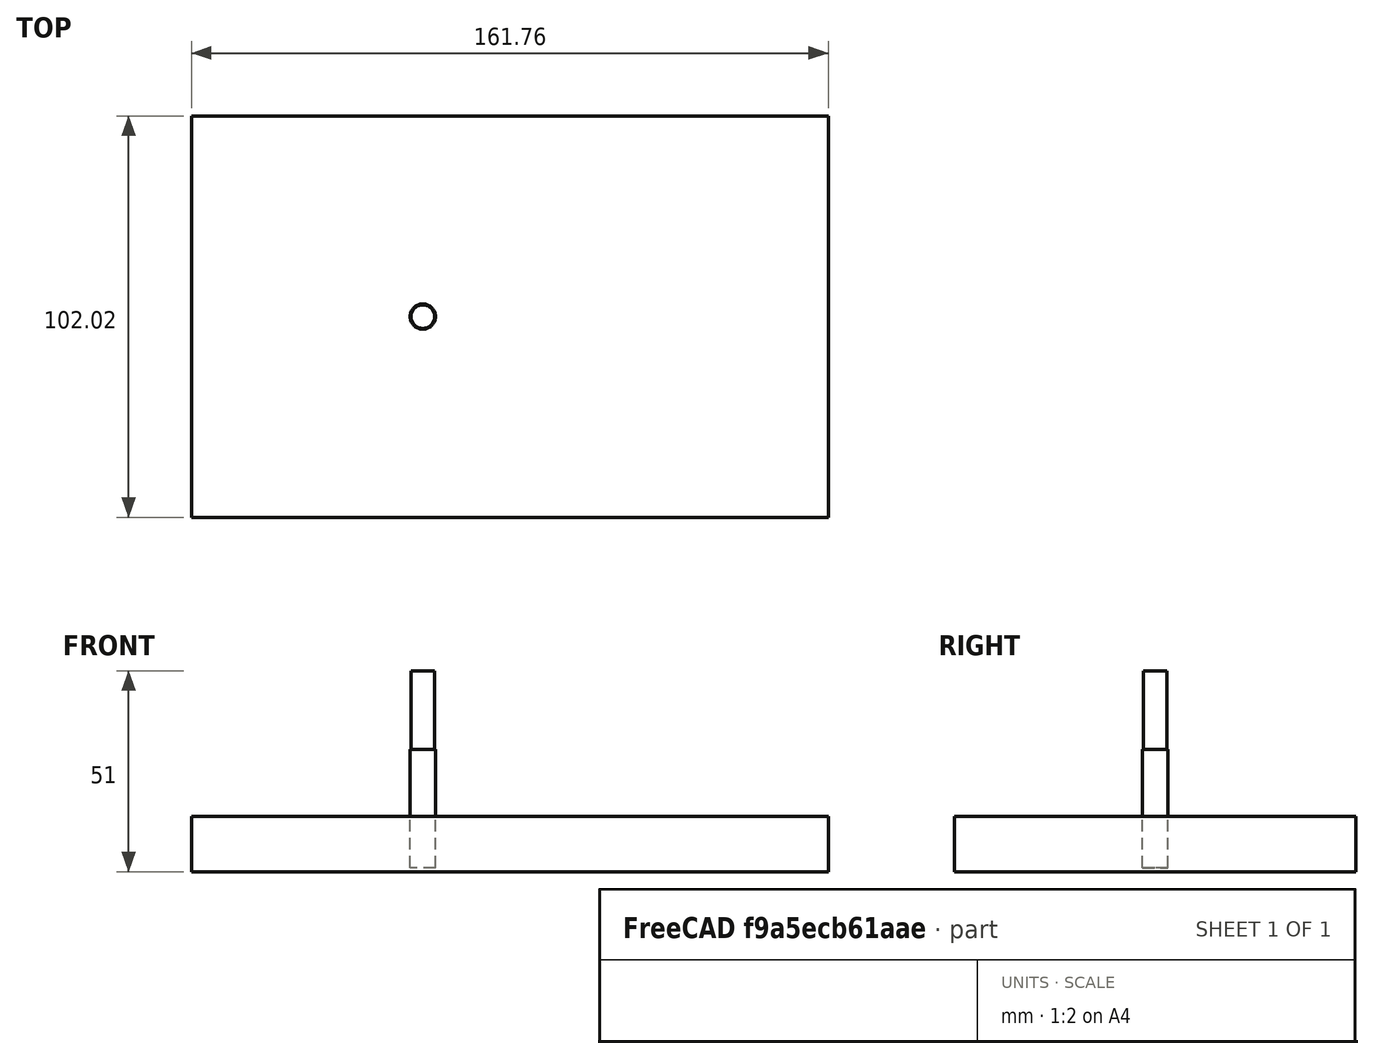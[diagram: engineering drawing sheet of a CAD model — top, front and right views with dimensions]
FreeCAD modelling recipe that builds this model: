
FCSTD DOCUMENT  (FreeCAD 0.20R27465 (Git))
Label: DemoFit
License: All rights reserved
LicenseURL: http://en.wikipedia.org/wiki/All_rights_reserved
objects: Part::FeaturePython×5, Path::FeaturePython×5, Sketcher::SketchObject×3, PartDesign::Pad×3, PartDesign::Fillet×3, PartDesign::Body×3, Mesh::FeaturePython×3, App::DocumentObjectGroup×2, App::FeaturePython×1, Path::FeatureCompoundPython×1
note: 26 computed .brp shape members not serialized (recipe doc carries the construction recipe); baked Part::Feature solids carry a one-line shape summary decoded from their .brp

FEATURE [Sketcher::SketchObject] Sketch
  FullyConstrained = true
  MapMode = 5
  Support = -> [XY_Plane]
  sketch-geometry (24):
    g0: LineSegment StartX=-57.735 StartY=0 StartZ=0 EndX=-28.8675 EndY=-50 EndZ=0
    g1: LineSegment StartX=-28.8675 StartY=-50 StartZ=0 EndX=28.8675 EndY=-50 EndZ=0
    g2: LineSegment StartX=28.8675 StartY=-50 StartZ=0 EndX=57.735 EndY=0 EndZ=0
    g3: LineSegment StartX=57.735 StartY=0 StartZ=0 EndX=28.8675 EndY=50 EndZ=0
    g4: LineSegment StartX=28.8675 StartY=50 StartZ=0 EndX=-28.8675 EndY=50 EndZ=0
    g5: LineSegment StartX=-28.8675 StartY=50 StartZ=0 EndX=-57.735 EndY=0 EndZ=0
    g6: Circle CenterX=0 CenterY=0 CenterZ=0 NormalX=0 NormalY=0 NormalZ=1 AngleXU=0 Radius=57.735
    g7: LineSegment StartX=-30.0067 StartY=21.9359 StartZ=0 EndX=-45.2718 EndY=9.76238 EndZ=0
    g8: LineSegment StartX=-45.2718 StartY=9.76238 StartZ=0 EndX=-45.2718 EndY=-9.76238 EndZ=0
    g9: LineSegment StartX=-45.2718 StartY=-9.76238 StartZ=0 EndX=-30.0067 EndY=-21.9359 EndZ=0
    g10: LineSegment StartX=-30.0067 StartY=-21.9359 StartZ=0 EndX=-10.9715 EndY=-17.5912 EndZ=0
    g11: LineSegment StartX=-10.9715 StartY=-17.5912 StartZ=0 EndX=-2.5 EndY=0 EndZ=0
    g12: LineSegment StartX=-2.5 StartY=0 StartZ=0 EndX=-10.9715 EndY=17.5912 EndZ=0
    g13: LineSegment StartX=-10.9715 StartY=17.5912 StartZ=0 EndX=-30.0067 EndY=21.9359 EndZ=0
    g14: Circle CenterX=-25 CenterY=0 CenterZ=0 NormalX=0 NormalY=0 NormalZ=1 AngleXU=0 Radius=22.5
    g15: LineSegment StartX=25 StartY=22.5 StartZ=0 EndX=9.0901 EndY=15.9099 EndZ=0
    g16: LineSegment StartX=9.0901 StartY=15.9099 StartZ=0 EndX=2.5 EndY=0 EndZ=0
    g17: LineSegment StartX=2.5 StartY=0 StartZ=0 EndX=9.0901 EndY=-15.9099 EndZ=0
    g18: LineSegment StartX=9.0901 StartY=-15.9099 StartZ=0 EndX=25 EndY=-22.5 EndZ=0
    g19: LineSegment StartX=25 StartY=-22.5 StartZ=0 EndX=40.9099 EndY=-15.9099 EndZ=0
    g20: LineSegment StartX=40.9099 StartY=-15.9099 StartZ=0 EndX=47.5 EndY=-3.6e-15 EndZ=0
    g21: LineSegment StartX=47.5 StartY=-3.6e-15 StartZ=0 EndX=40.9099 EndY=15.9099 EndZ=0
    g22: LineSegment StartX=40.9099 StartY=15.9099 StartZ=0 EndX=25 EndY=22.5 EndZ=0
    g23: Circle CenterX=25 CenterY=0 CenterZ=0 NormalX=0 NormalY=0 NormalZ=1 AngleXU=0 Radius=22.5
  constraints (56):
    c: Coincident(g0,g1)
    c: Coincident(g1,g2)
    c: Coincident(g2,g3)
    c: Coincident(g3,g4)
    c: Coincident(g4,g5)
    c: Coincident(g5,g0)
    c: Equal(g0, g1-g5) x5
    c: PointOnObject(g0,g6)
    c: PointOnObject(g1,g6)
    c: PointOnObject(g2,g6)
    c: PointOnObject(g3,g6)
    c: PointOnObject(g4,g6)
    c: PointOnObject(g5,g6)
    c: Coincident(g6,g-1)
    c: DistanceY(g-1,g2) = 0
    c: DistanceY(g-1,g4) = 50
    c: Coincident(g7,g8)
    c: Coincident(g8,g9)
    c: Coincident(g9,g10)
    c: Coincident(g10,g11)
    c: Coincident(g11,g12)
    c: Coincident(g12,g13)
    c: Coincident(g13,g7)
    c: Equal(g7, g8-g13) x6
    c: PointOnObject(g7,g14)
    c: PointOnObject(g8,g14)
    c: PointOnObject(g9,g14)
    c: PointOnObject(g10,g14)
    c: PointOnObject(g11,g14)
    c: PointOnObject(g12,g14)
    c: PointOnObject(g13,g14)
    c: DistanceY(g-1,g14) = 0
    c: DistanceX(g14,g-1) = 25
    c: Diameter(g14) = 45
    c: DistanceY(g-1,g11) = 0
    c: Coincident(g15,g16)
    c: Coincident(g16,g17)
    c: Coincident(g17,g18)
    c: Coincident(g18,g19)
    c: Coincident(g19,g20)
    c: Coincident(g20,g21)
    c: Coincident(g21,g22)
    c: Coincident(g22,g15)
    c: Equal(g15, g16-g22) x7
    c: PointOnObject(g15,g23)
    c: PointOnObject(g16,g23)
    c: PointOnObject(g17,g23)
    c: PointOnObject(g18,g23)
    c: PointOnObject(g19,g23)
    c: PointOnObject(g20,g23)
    c: PointOnObject(g21,g23)
    c: PointOnObject(g22,g23)
    c: DistanceX(g-1,g23) = 25
    c: DistanceY(g-1,g23) = 0
    c: Diameter(g23) = 45
    c: DistanceY(g-1,g16) = 0
FEATURE [PartDesign::Pad] Pad
  Direction = (1,1,1)
  Length = 12
  Length2 = 100
  Profile = -> Sketch
  Refine = true
  Type = 0
FEATURE [Sketcher::SketchObject] Sketch001
  FullyConstrained = true
  MapMode = 5
  Support = -> [XY_Plane001]
  sketch-geometry (8):
    g0: LineSegment StartX=100.227 StartY=15.2593 StartZ=0 EndX=100.227 EndY=34.7407 EndZ=0
    g1: LineSegment StartX=100.227 StartY=34.7407 StartZ=0 EndX=84.9956 EndY=46.8871 EndZ=0
    g2: LineSegment StartX=84.9956 StartY=46.8871 StartZ=0 EndX=66.0027 EndY=42.5521 EndZ=0
    g3: LineSegment StartX=66.0027 StartY=42.5521 StartZ=0 EndX=57.55 EndY=25 EndZ=0
    g4: LineSegment StartX=57.55 StartY=25 StartZ=0 EndX=66.0027 EndY=7.44788 EndZ=0
    g5: LineSegment StartX=66.0027 StartY=7.44788 StartZ=0 EndX=84.9956 EndY=3.11287 EndZ=0
    g6: LineSegment StartX=84.9956 StartY=3.11287 StartZ=0 EndX=100.227 EndY=15.2593 EndZ=0
    g7: Circle CenterX=80 CenterY=25 CenterZ=0 NormalX=0 NormalY=0 NormalZ=1 AngleXU=0 Radius=22.45
  constraints (19):
    c: Coincident(g0,g1)
    c: Coincident(g1,g2)
    c: Coincident(g2,g3)
    c: Coincident(g3,g4)
    c: Coincident(g4,g5)
    c: Coincident(g5,g6)
    c: Coincident(g6,g0)
    c: Equal(g0, g1-g6) x6
    c: PointOnObject(g0,g7)
    c: PointOnObject(g1,g7)
    c: PointOnObject(g2,g7)
    c: PointOnObject(g3,g7)
    c: PointOnObject(g4,g7)
    c: PointOnObject(g5,g7)
    c: PointOnObject(g6,g7)
    c: DistanceX(g-1,g7) = 80
    c: DistanceY(g-1,g7) = 25
    c: Diameter(g7) = 44.9
    c: DistanceY(g-1,g3) = 25
FEATURE [PartDesign::Pad] Pad001
  Direction = (1,1,1)
  Length = 12
  Length2 = 100
  Profile = -> Sketch001
  Refine = true
  Type = 0
FEATURE [Sketcher::SketchObject] Sketch002
  FullyConstrained = true
  MapMode = 5
  Support = -> [XY_Plane002]
  sketch-geometry (9):
    g0: LineSegment StartX=102.249 StartY=-31 StartZ=0 EndX=97.8535 EndY=-14.3891 EndZ=0
    g1: LineSegment StartX=97.8535 StartY=-14.3891 StartZ=0 EndX=83 EndY=-5.75135 EndZ=0
    g2: LineSegment StartX=83 StartY=-5.75135 StartZ=0 EndX=66.3891 EndY=-10.1465 EndZ=0
    g3: LineSegment StartX=66.3891 StartY=-10.1465 StartZ=0 EndX=57.7513 EndY=-25 EndZ=0
    g4: LineSegment StartX=57.7513 StartY=-25 StartZ=0 EndX=62.1465 EndY=-41.6109 EndZ=0
    g5: LineSegment StartX=62.1465 StartY=-41.6109 StartZ=0 EndX=77 EndY=-50.2487 EndZ=0
    g6: LineSegment StartX=77 StartY=-50.2487 StartZ=0 EndX=93.6109 EndY=-45.8535 EndZ=0
    g7: LineSegment StartX=93.6109 StartY=-45.8535 StartZ=0 EndX=102.249 EndY=-31 EndZ=0
    g8: Circle CenterX=80 CenterY=-28 CenterZ=0 NormalX=0 NormalY=0 NormalZ=1 AngleXU=0 Radius=22.45
  constraints (21):
    c: Coincident(g0,g1)
    c: Coincident(g1,g2)
    c: Coincident(g2,g3)
    c: Coincident(g3,g4)
    c: Coincident(g4,g5)
    c: Coincident(g5,g6)
    c: Coincident(g6,g7)
    c: Coincident(g7,g0)
    c: Equal(g0, g1-g7) x7
    c: PointOnObject(g0,g8)
    c: PointOnObject(g1,g8)
    c: PointOnObject(g2,g8)
    c: PointOnObject(g3,g8)
    c: PointOnObject(g4,g8)
    c: PointOnObject(g5,g8)
    c: PointOnObject(g6,g8)
    c: PointOnObject(g7,g8)
    c: DistanceY(g8,g-1) = 28
    c: Diameter(g8) = 44.9
    c: DistanceY(g3,g-1) = 25
    c: DistanceX(g-1,g8) = 80
FEATURE [PartDesign::Pad] Pad002
  Direction = (1,1,1)
  Length = 12
  Length2 = 100
  Profile = -> Sketch002
  Refine = true
  Type = 0
FEATURE [PartDesign::Fillet] Fillet
  Base = -> Pad002 [Edge14,Edge17,Edge20,Edge1,Edge11,Edge8,Edge5,Edge2]
  BaseFeature = -> Pad002
  Radius = 3.2
  Refine = true
  SupportTransform = false
  UseAllEdges = false
FEATURE [PartDesign::Body] Body002  label="Hexagon"
  Group = -> [Sketch002,Pad002,Fillet]
  Origin = -> Origin002
  Tip = -> Fillet
FEATURE [PartDesign::Fillet] Fillet001
  Base = -> Pad001 [Edge8,Edge5,Edge2,Edge1,Edge11,Edge14,Edge17]
  BaseFeature = -> Pad001
  Radius = 3.2
  Refine = true
  SupportTransform = false
  UseAllEdges = false
FEATURE [PartDesign::Body] Body001  label="Heptagon"
  Group = -> [Sketch001,Pad001,Fillet001]
  Origin = -> Origin001
  Tip = -> Fillet001
FEATURE [PartDesign::Fillet] Fillet002
  Base = -> Pad [Edge44,Edge43,Edge59,Edge38,Edge20,Edge19,Edge56,Edge53,Edge35,Edge32,Edge29,Edge50,Edge47,Edge26,Edge23]
  BaseFeature = -> Pad
  Radius = 3.2
  Refine = true
  SupportTransform = false
  UseAllEdges = false
FEATURE [PartDesign::Body] Body  label="Main Body"
  Group = -> [Sketch,Pad,Fillet002]
  Origin = -> Origin
  Tip = -> Fillet002
FEATURE [App::FeaturePython] SetupSheet  # Path/CAM operation (typed FeaturePython)
  ClearanceHeightExpression = OpStockZMax+SetupSheet.ClearanceHeightOffset
  ClearanceHeightOffset = 5
  CoolantMode = 0
  CoolantModes = None | Flood | Mist
  FinalDepthExpression = OpFinalDepth
  HorizRapid = 0
  SafeHeightExpression = OpStockZMax+SetupSheet.SafeHeightOffset
  SafeHeightOffset = 3
  StartDepthExpression = OpStartDepth
  StepDownExpression = OpToolDiameter
  VertRapid = 0
FEATURE [Part::FeaturePython] Clone  label="Model-Heptagon"  # Draft clone (typed FeaturePython)
  AttacherType = Attacher::AttachEngine3D
  Fuse = false
  Objects = -> [Body001]
  PathResource = Model
  Scale = (1,1,1)
FEATURE [Part::FeaturePython] Clone001  label="Model-Hexagon"  # Draft clone (typed FeaturePython)
  AttacherType = Attacher::AttachEngine3D
  Fuse = false
  Objects = -> [Body002]
  PathResource = Model
  Scale = (1,1,1)
FEATURE [Part::FeaturePython] Clone002  label="Model-Main Body"  # Draft clone (typed FeaturePython)
  AttacherType = Attacher::AttachEngine3D
  Fuse = false
  Objects = -> [Body]
  PathResource = Model
  Scale = (1,1,1)
FEATURE [App::DocumentObjectGroup] Model
  Group = -> [Clone,Clone001,Clone002]
FEATURE [Part::FeaturePython] Stock  # WARN: FeaturePython — macro-defined, semantics opaque (R4)
  Base = -> Model
  ExtXneg = 1
  ExtXpos = 1
  ExtYneg = 1
  ExtYpos = 1
  ExtZneg = 1
  ExtZpos = 1
  Placement = pos=(-57.735,-50.0158,0) rot=(0,0,1;0rad)
  StockType = FromBase
FEATURE [Part::FeaturePython] ToolBit001  label="6.4mm Endmill"  # Path/CAM toolbit (typed FeaturePython)
  BitPropertyNames = Chipload | CuttingEdgeHeight | Diameter | Flutes | Length | Material | ShankDiameter
  BitShape = /app/freecad/Mod/Path/Tools/Shape/endmill.fcstd
  Chipload = 0
  CuttingEdgeHeight = 30
  Diameter = 6.4
  File = <userpath>/Documents/CNCRouter/FreeCAD/Bit/6.4mm_Endmill.fctb
  Flutes = 0
  Length = 50
  Material = 0
  ShankDiameter = 6
  ShapeName = endmill
FEATURE [Path::FeaturePython] __4mm_Endmill  label="6.4mm Endmill001"  # Path/CAM operation (typed FeaturePython)
  HorizFeed = 50
  HorizRapid = 0
  SpindleDir = 0
  SpindleSpeed = 10000
  Tool = -> ToolBit001
  ToolNumber = 2
  VertFeed = 50
  VertRapid = 0
  expr: HorizRapid = SetupSheet.HorizRapid
  expr: VertRapid = SetupSheet.VertRapid
FEATURE [App::DocumentObjectGroup] Tools
  Group = -> [__4mm_Endmill]
FEATURE [Path::FeaturePython] Profile  # Path/CAM operation (typed FeaturePython)
  Active = true
  AreaParams:
    Tolerance = 1e-07
    FitArcs = True
    Simplify = False
    CleanDistance = 0.0
    Accuracy = 0.01
    Unit = 1.0
    MinArcPoints = 4
    MaxArcPoints = 100
    ClipperScale = 10000000.0
    Fill = 0
    Coplanar = 0
    Reorient = True
    Outline = False
    Explode = False
    OpenMode = 0
    Deflection = 0.01
    SubjectFill = 0
    ClipFill = 0
    Offset = 3.2
    ExtraPass = 0
    Stepover = 0.0
    LastStepover = 0.0
    JoinType = 0
    EndType = 0
    MiterLimit = 2.0
    RoundPrecision = 0.0
    PocketMode = 0
    ToolRadius = 1.0
    PocketExtraOffset = 0.0
    PocketStepover = 0.0
    PocketLastStepover = 0.0
    FromCenter = False
    Angle = 45.0
    AngleShift = 0.0
    Shift = 0.0
    Thicken = False
    SectionCount = -1
    Stepdown = 1.0
    SectionOffset = 0.0
    SectionTolerance = 1e-06
    SectionMode = 2
    Project = False
  AttemptInverseAngle = true
  Base = -> [Clone002,Clone,Clone001]
  ClearanceHeight = 18
  CoolantMode = 0
  CycleTime = 00:00:43
  Direction = 0
  EnableRotation = 0
  FinalDepth = 0
  HandleMultipleFeatures = 0
  InverseAngle = false
  JoinType = 0
  LimitDepthToFace = true
  MiterLimit = 0.1
  OffsetExtra = 0
  OpFinalDepth = 12
  OpStartDepth = 13
  OpStockZMax = 13
  OpStockZMin = -1
  OpToolDiameter = 6.4
  PathParams = {'orientation': 1, 'feedrate': 50.0, 'feedrate_v': 50.0, 'verbose': True, 'resume_height': 16.0, 'retraction': 18.0, 'return_end': True, 'preamble': False, 'start': Vector (56.95676904267071, 31.12767782850635, 18.0)}
  ReverseDirection = false
  SafeHeight = 16
  Side = 0
  SplitArcs = false
  StartDepth = 12
  StartPoint = (0,0,0)
  StepDown = 5
  ToolController = -> __4mm_Endmill
  UseComp = true
  UseStartPoint = false
  processCircles = false
  processHoles = false
  processPerimeter = true
  expr: ClearanceHeight = OpStockZMax + SetupSheet.ClearanceHeightOffset
  expr: SafeHeight = OpStockZMax + SetupSheet.SafeHeightOffset
  expr: StartDepth = 12
  expr: StepDown = 5
FEATURE [Mesh::FeaturePython] CutMaterial  # WARN: FeaturePython — macro-defined, semantics opaque (R4)
FEATURE [Path::FeaturePython] Profile001  # Path/CAM operation (typed FeaturePython)
  Active = true
  AreaParams:
    Tolerance = 1e-07
    FitArcs = True
    Simplify = False
    CleanDistance = 0.0
    Accuracy = 0.01
    Unit = 1.0
    MinArcPoints = 4
    MaxArcPoints = 100
    ClipperScale = 10000000.0
    Fill = 0
    Coplanar = 0
    Reorient = True
    Outline = False
    Explode = False
    OpenMode = 0
    Deflection = 0.01
    SubjectFill = 0
    ClipFill = 0
    Offset = -3.2
    ExtraPass = 0
    Stepover = 0.0
    LastStepover = 0.0
    JoinType = 0
    EndType = 0
    MiterLimit = 2.0
    RoundPrecision = 0.0
    PocketMode = 0
    ToolRadius = 1.0
    PocketExtraOffset = 0.0
    PocketStepover = 0.0
    PocketLastStepover = 0.0
    FromCenter = False
    Angle = 45.0
    AngleShift = 0.0
    Shift = 0.0
    Thicken = False
    SectionCount = -1
    Stepdown = 1.0
    SectionOffset = 0.0
    SectionTolerance = 1e-06
    SectionMode = 2
    Project = False
  AttemptInverseAngle = true
  Base = -> [Clone002]
  ClearanceHeight = 18
  CoolantMode = 0
  CycleTime = 00:00:08
  Direction = 0
  EnableRotation = 0
  FinalDepth = 0
  HandleMultipleFeatures = 0
  InverseAngle = false
  JoinType = 0
  LimitDepthToFace = true
  MiterLimit = 0.1
  OffsetExtra = 0
  OpFinalDepth = 0
  OpStartDepth = 13
  OpStockZMax = 13
  OpStockZMin = -1
  OpToolDiameter = 6.4
  PathParams = {'orientation': 1, 'feedrate': 50.0, 'feedrate_v': 50.0, 'verbose': True, 'resume_height': 16.0, 'retraction': 18.0, 'return_end': True, 'preamble': False}
  ReverseDirection = false
  SafeHeight = 16
  Side = 1
  SplitArcs = false
  StartDepth = 13
  StartPoint = (0,0,0)
  StepDown = 6.4
  ToolController = -> __4mm_Endmill
  UseComp = true
  UseStartPoint = false
  processCircles = false
  processHoles = false
  processPerimeter = true
  expr: ClearanceHeight = OpStockZMax + SetupSheet.ClearanceHeightOffset
  expr: FinalDepth = OpFinalDepth
  expr: SafeHeight = OpStockZMax + SetupSheet.SafeHeightOffset
  expr: StartDepth = OpStartDepth
  expr: StepDown = OpToolDiameter
FEATURE [Path::FeaturePython] Profile002  # Path/CAM operation (typed FeaturePython)
  Active = true
  AreaParams:
    Tolerance = 1e-07
    FitArcs = True
    Simplify = False
    CleanDistance = 0.0
    Accuracy = 0.01
    Unit = 1.0
    MinArcPoints = 4
    MaxArcPoints = 100
    ClipperScale = 10000000.0
    Fill = 0
    Coplanar = 0
    Reorient = True
    Outline = False
    Explode = False
    OpenMode = 0
    Deflection = 0.01
    SubjectFill = 0
    ClipFill = 0
    Offset = -3.2
    ExtraPass = 0
    Stepover = 0.0
    LastStepover = 0.0
    JoinType = 0
    EndType = 0
    MiterLimit = 2.0
    RoundPrecision = 0.0
    PocketMode = 0
    ToolRadius = 1.0
    PocketExtraOffset = 0.0
    PocketStepover = 0.0
    PocketLastStepover = 0.0
    FromCenter = False
    Angle = 45.0
    AngleShift = 0.0
    Shift = 0.0
    Thicken = False
    SectionCount = -1
    Stepdown = 1.0
    SectionOffset = 0.0
    SectionTolerance = 1e-06
    SectionMode = 2
    Project = False
  AttemptInverseAngle = true
  Base = -> [Clone002]
  ClearanceHeight = 18
  CoolantMode = 0
  CycleTime = 00:00:08
  Direction = 0
  EnableRotation = 0
  FinalDepth = 0
  HandleMultipleFeatures = 0
  InverseAngle = false
  JoinType = 0
  LimitDepthToFace = true
  MiterLimit = 0.1
  OffsetExtra = 0
  OpFinalDepth = 0
  OpStartDepth = 13
  OpStockZMax = 13
  OpStockZMin = -1
  OpToolDiameter = 6.4
  PathParams = {'orientation': 1, 'feedrate': 50.0, 'feedrate_v': 50.0, 'verbose': True, 'resume_height': 16.0, 'retraction': 18.0, 'return_end': True, 'preamble': False}
  ReverseDirection = false
  SafeHeight = 16
  Side = 1
  SplitArcs = false
  StartDepth = 13
  StartPoint = (0,0,0)
  StepDown = 6.4
  ToolController = -> __4mm_Endmill
  UseComp = true
  UseStartPoint = false
  processCircles = false
  processHoles = false
  processPerimeter = true
  expr: ClearanceHeight = OpStockZMax + SetupSheet.ClearanceHeightOffset
  expr: FinalDepth = OpFinalDepth
  expr: SafeHeight = OpStockZMax + SetupSheet.SafeHeightOffset
  expr: StartDepth = OpStartDepth
  expr: StepDown = OpToolDiameter
FEATURE [Path::FeatureCompoundPython] Operations  # Path/CAM operation (typed FeaturePython)
  Group = -> [Profile001,Profile002,Profile]
  UsePlacements = false
FEATURE [Path::FeaturePython] Job  # Path/CAM operation (typed FeaturePython)
  CycleTime = 00:00:59
  Fixtures = G54
  GeometryTolerance = 0.01
  JobType = 0
  LastPostProcessDate = 2022-02-21 13:16:16.731527
  LastPostProcessOutput = <userpath>/MensShed/CNCRouter/Shapes/DemoFit.ngc
  Model = -> Model
  Operations = -> Operations
  OrderOutputBy = 0
  PostProcessor = 7
  PostProcessorOutputFile = %D/%d.ngc
  SetupSheet = -> SetupSheet
  SplitOutput = false
  Stock = -> Stock
  Tools = -> Tools
FEATURE [Mesh::FeaturePython] CutMaterial001  # WARN: FeaturePython — macro-defined, semantics opaque (R4)
FEATURE [Mesh::FeaturePython] CutMaterial002  # WARN: FeaturePython — macro-defined, semantics opaque (R4)
